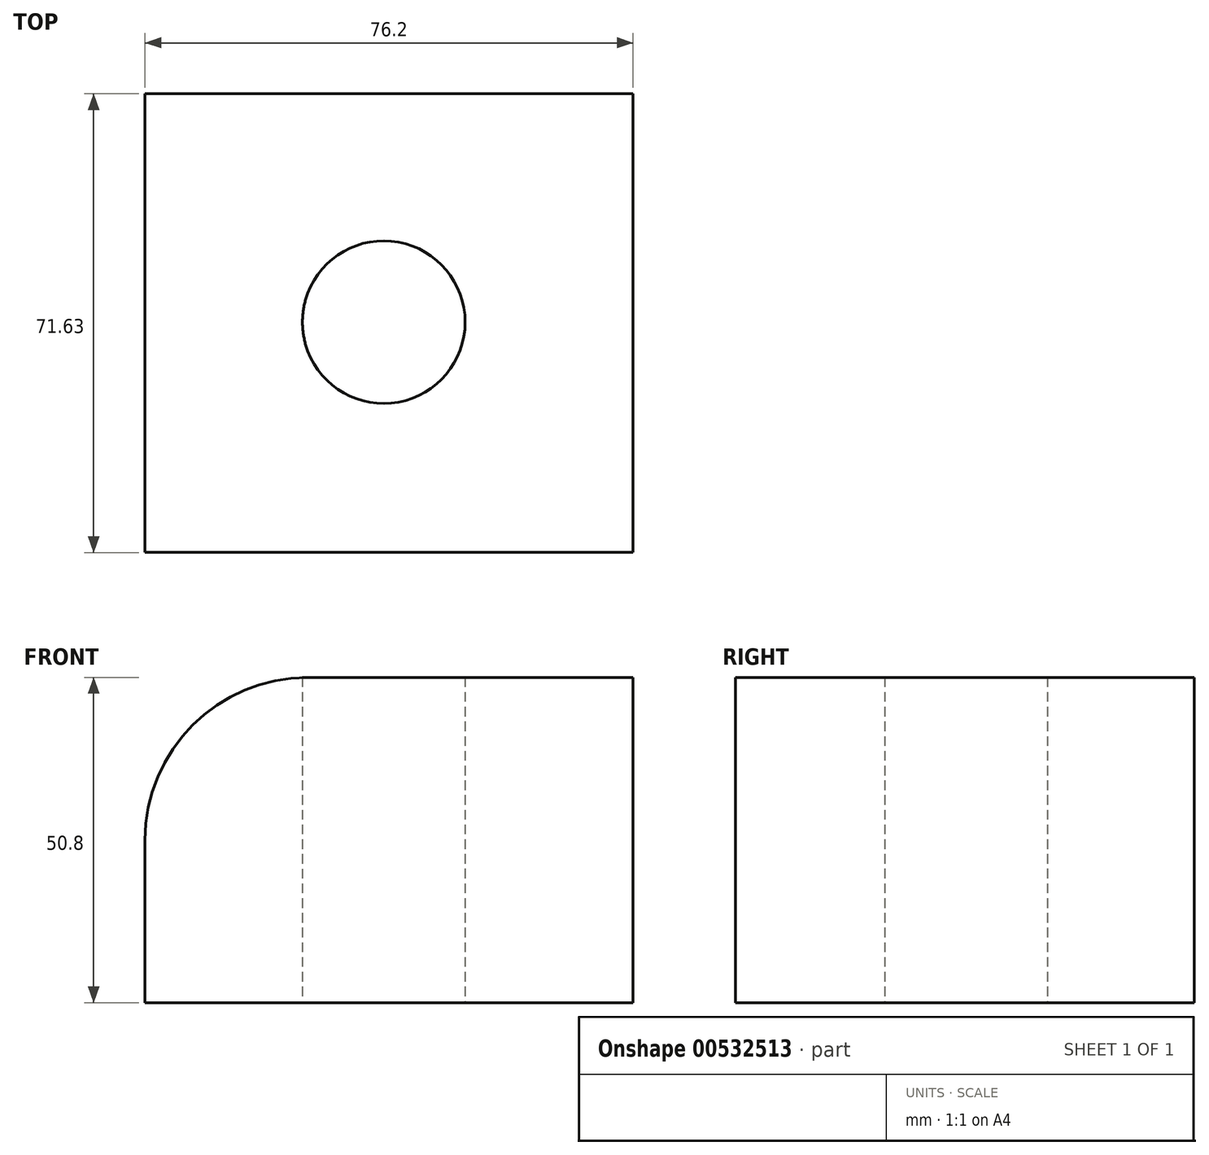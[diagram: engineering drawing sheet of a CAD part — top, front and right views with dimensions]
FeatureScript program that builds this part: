
annotation { "Feature Type Name" : "Feature", "Feature Type Description" : "" }
export const myFeature = defineFeature(function(context is Context, id is Id, definition is map)
    precondition{}
    {
        {
            var Q0;
            Q0=qCreatedBy(makeId("Front.planeOp"),FACE);
            var sketch = newSketch(context, id + "F0", { "sketchPlane" : qUnion([Q0])});
            skLineSegment(sketch, "E0.bottom", {"start": v(0, 0) * mm, "end": v(-76.2, 0) * mm});
            skLineSegment(sketch, "E0.top", {"start": v(0, 50.8) * mm, "end": v(-50.8, 50.8) * mm});
            skLineSegment(sketch, "E0.left", {"start": v(0, 0) * mm, "end": v(0, 50.8) * mm});
            skLineSegment(sketch, "E0.right", {"start": v(-76.2, 0) * mm, "end": v(-76.2, 25.4) * mm});
            skPoint(sketch, "E1.visualSharp", {"position": v(-76.2, 50.8) * mm});
            skArc(sketch, "E1.filletArc", {"start": v(-50.8, 50.8) * mm, "mid": v(-68.76, 43.36) * mm, "end": v(-76.2, 25.4) * mm});
            skSolve(sketch);
        }
        {
            var Q0;
            Q0=makeQuery(id+"F0.imprint","IMPRINT",FACE,{"disambiguationData":[TD([[makeQuery(id+"F0.imprint","IMPRINT",EDGE,{"derivedFrom":sQuery(id+"F0.wireOp",EDGE,"E0.bottom")}),-1.0]])]});
            extrude(context, id + "F1", {"entities" : qUnion([Q0]), "depth" : 71.63 * mm, "offsetDistance" : 25.4 * mm});
        }
        {
            var Q0;
            Q0=makeQuery(id+"F1.opExtrude","SWEPT_FACE",FACE,{"disambiguationData":[OSD([sQuery(id+"F0.wireOp",EDGE,"E0.bottom")])]});
            var sketch = newSketch(context, id + "F2", { "sketchPlane" : qUnion([Q0])});
            skCircle(sketch, "E2", {"center": v(-38.92, 35.65) * mm, "radius": 12.7 * mm});
            skSolve(sketch);
        }
        {
            var Q0;
            Q0=makeQuery(id+"F2.imprint","IMPRINT",FACE,{"disambiguationData":[TD([[makeQuery(id+"F2.imprint","IMPRINT",EDGE,{"derivedFrom":sQuery(id+"F2.wireOp",EDGE,"E2")}),1.0]])]});
            extrude(context, id + "F3", {"entities" : qUnion([Q0]), "operationType" : NewBodyOperationType.REMOVE, "endBound" : BoundingType.THROUGH_ALL, "oppositeDirection" : true, "depth" : 25.4 * mm, "offsetDistance" : 25.4 * mm});
        }
    });
